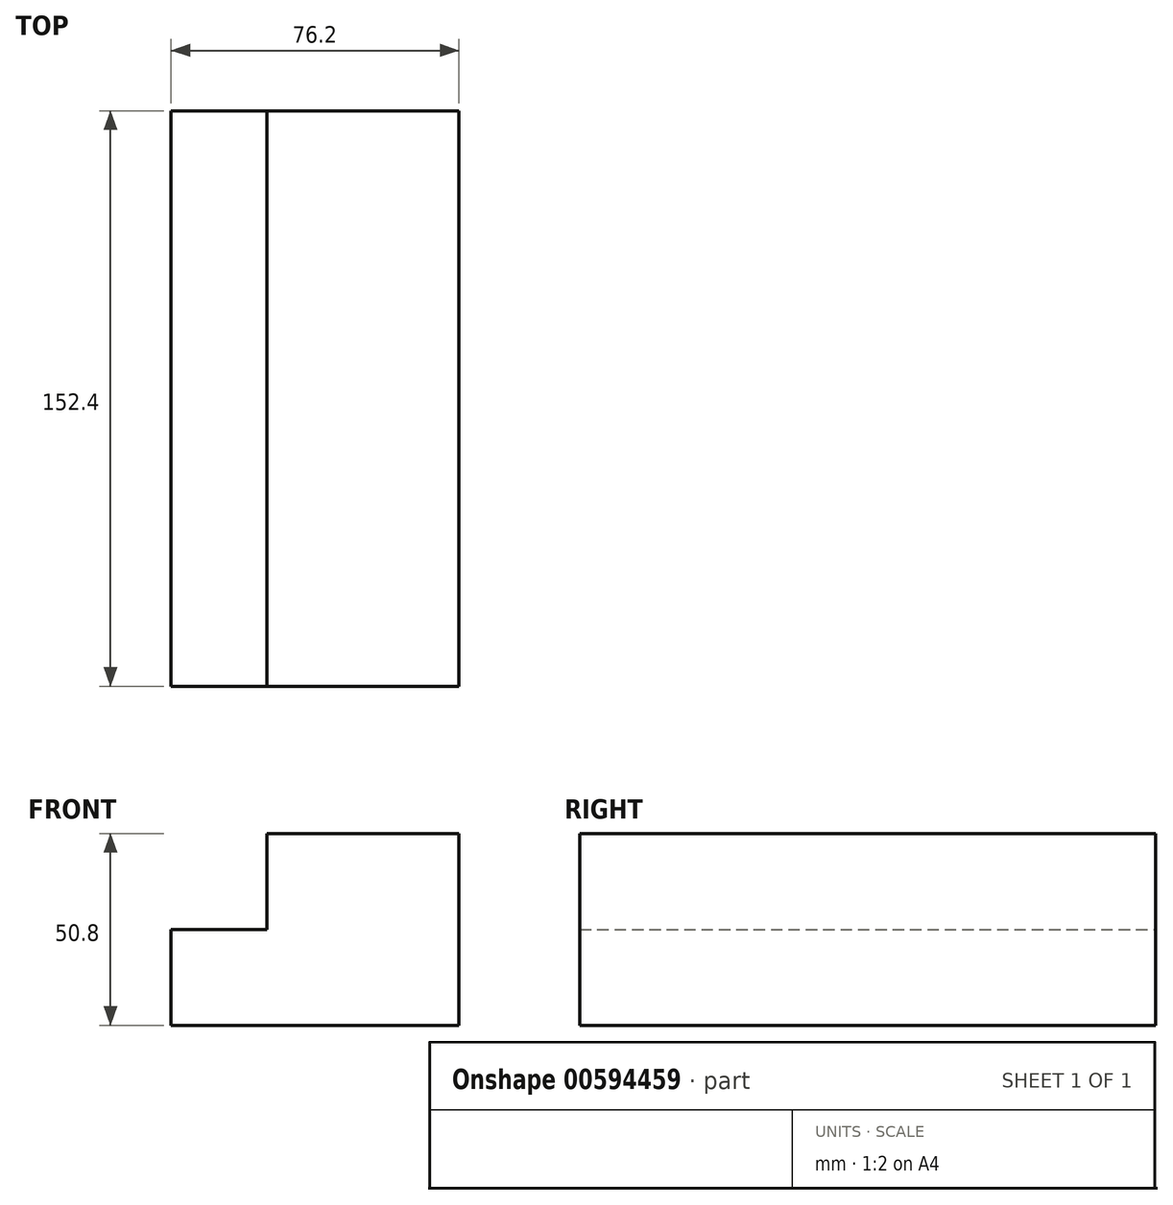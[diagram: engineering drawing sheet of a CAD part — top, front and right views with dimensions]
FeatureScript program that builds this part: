
annotation { "Feature Type Name" : "Feature", "Feature Type Description" : "" }
export const myFeature = defineFeature(function(context is Context, id is Id, definition is map)
    precondition{}
    {
        {
            var Q0;
            Q0=qCreatedBy(makeId("Front.planeOp"),FACE);
            var sketch = newSketch(context, id + "F0", { "sketchPlane" : qUnion([Q0])});
            skLineSegment(sketch, "E0", {"start": v(0, 0) * mm, "end": v(0, 25.4) * mm});
            skLineSegment(sketch, "E1", {"start": v(0, 25.4) * mm, "end": v(25.4, 25.4) * mm});
            skLineSegment(sketch, "E2", {"start": v(25.4, 25.4) * mm, "end": v(25.4, 50.8) * mm});
            skLineSegment(sketch, "E3", {"start": v(25.4, 50.8) * mm, "end": v(76.2, 50.8) * mm});
            skLineSegment(sketch, "E4", {"start": v(76.2, 50.8) * mm, "end": v(76.2, 0) * mm});
            skLineSegment(sketch, "E5", {"start": v(0, 0) * mm, "end": v(76.2, 0) * mm});
            skSolve(sketch);
        }
        {
            var Q0;
            Q0 = qSketchRegion(id + "F0", true);
            extrude(context, id + "F1", {"entities" : qUnion([Q0]), "depth" : 152.4 * mm, "offsetDistance" : 25.4 * mm});
        }
    });
